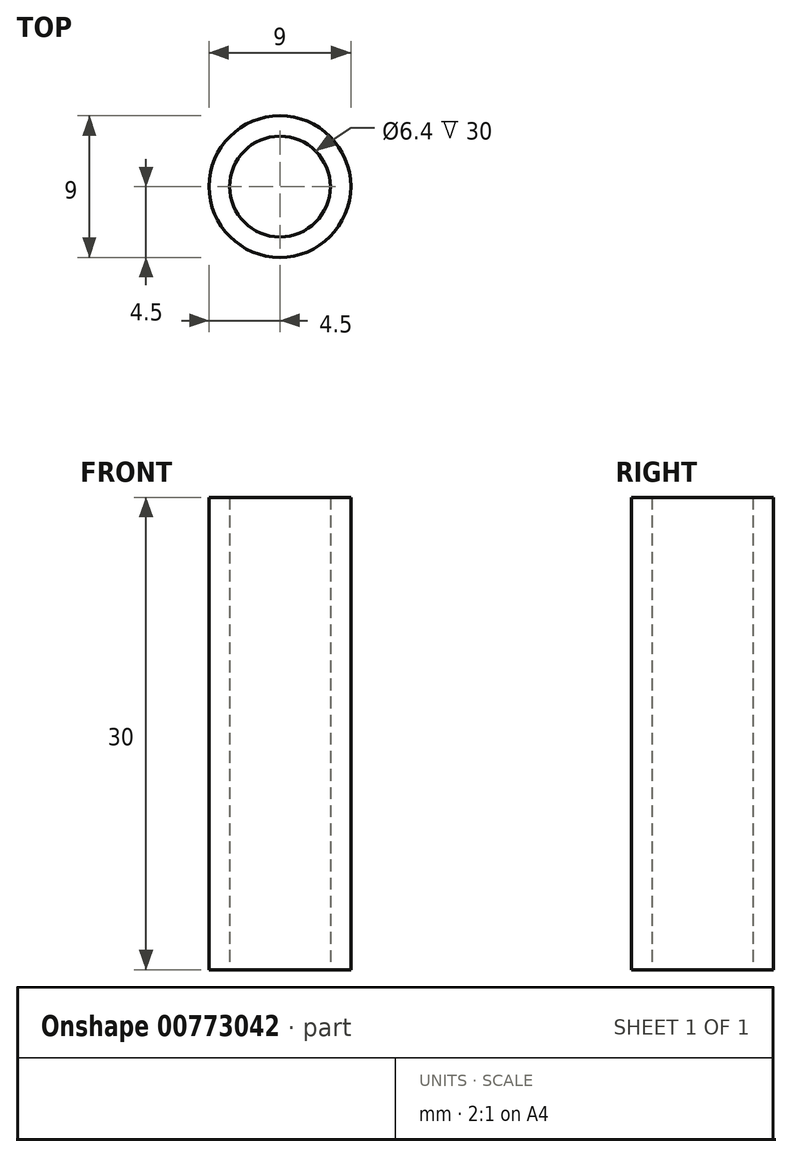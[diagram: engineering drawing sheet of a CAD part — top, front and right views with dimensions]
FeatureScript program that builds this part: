
annotation { "Feature Type Name" : "Feature", "Feature Type Description" : "" }
export const myFeature = defineFeature(function(context is Context, id is Id, definition is map)
    precondition{}
    {
        {
            var Q0;
            Q0=qCreatedBy(makeId("Top.planeOp"),FACE);
            var sketch = newSketch(context, id + "F0", { "sketchPlane" : qUnion([Q0])});
            skCircle(sketch, "E0", {"center": v(0, 0) * mm, "radius": 4.5 * mm});
            skCircle(sketch, "E1", {"center": v(0, 0) * mm, "radius": 3.2 * mm});
            skSolve(sketch);
        }
        {
            var Q0;
            Q0=makeQuery(id+"F0.imprint","IMPRINT",FACE,{"disambiguationData":[TD([[makeQuery(id+"F0.imprint","IMPRINT",EDGE,{"derivedFrom":sQuery(id+"F0.wireOp",EDGE,"E0")}),1.0]])]});
            extrude(context, id + "F1", {"entities" : qUnion([Q0]), "depth" : (40 - 10) * mm, "offsetDistance" : 25 * mm});
        }
    });
